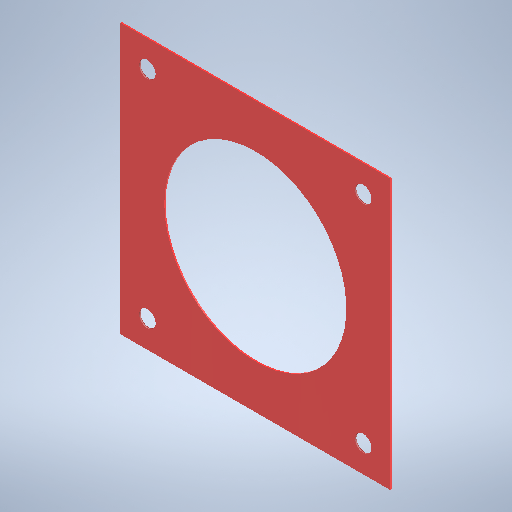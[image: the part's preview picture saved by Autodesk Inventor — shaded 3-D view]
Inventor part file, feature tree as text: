
AUTODESK INVENTOR PART (.ipt)
format: ipt  version: 2025 (Build 290162010, 162A)  size: 253,440 bytes
history: native  units: mm
features: sketch x2, extrude x1, hole x1
ambient origin geometry x8: Origin, YZ Plane, XZ Plane, XY Plane, X Axis, Y Axis, Z Axis, Center Point
bodies: Volumenkörper1 (feature_tree)
feature tree (4):
  extrude  "Extrusion1"  Depth=40.0mm
  hole  "Bohrung1"  [1 undecoded]
  sketch  "Skizze1"  dims[d0=40.0mm d1=40.0mm]
  sketch  "Skizze2"  dims[d2=27.0mm d3=0.2mm d4=0.0mm d5=2.459mm d6=6.0mm d7=4.0mm d8=2.0mm d9=90.0deg d10=10.5mm d11=0.0mm d12=32.0mm d13=16.0mm d14=32.0mm d15=16.0mm d16=20.0mm]
note: 1 required parameter value undecoded (feature->parameter linkage not recoverable at this tier; creation-order binding heuristic only, values carry confidence <= 0.55)
